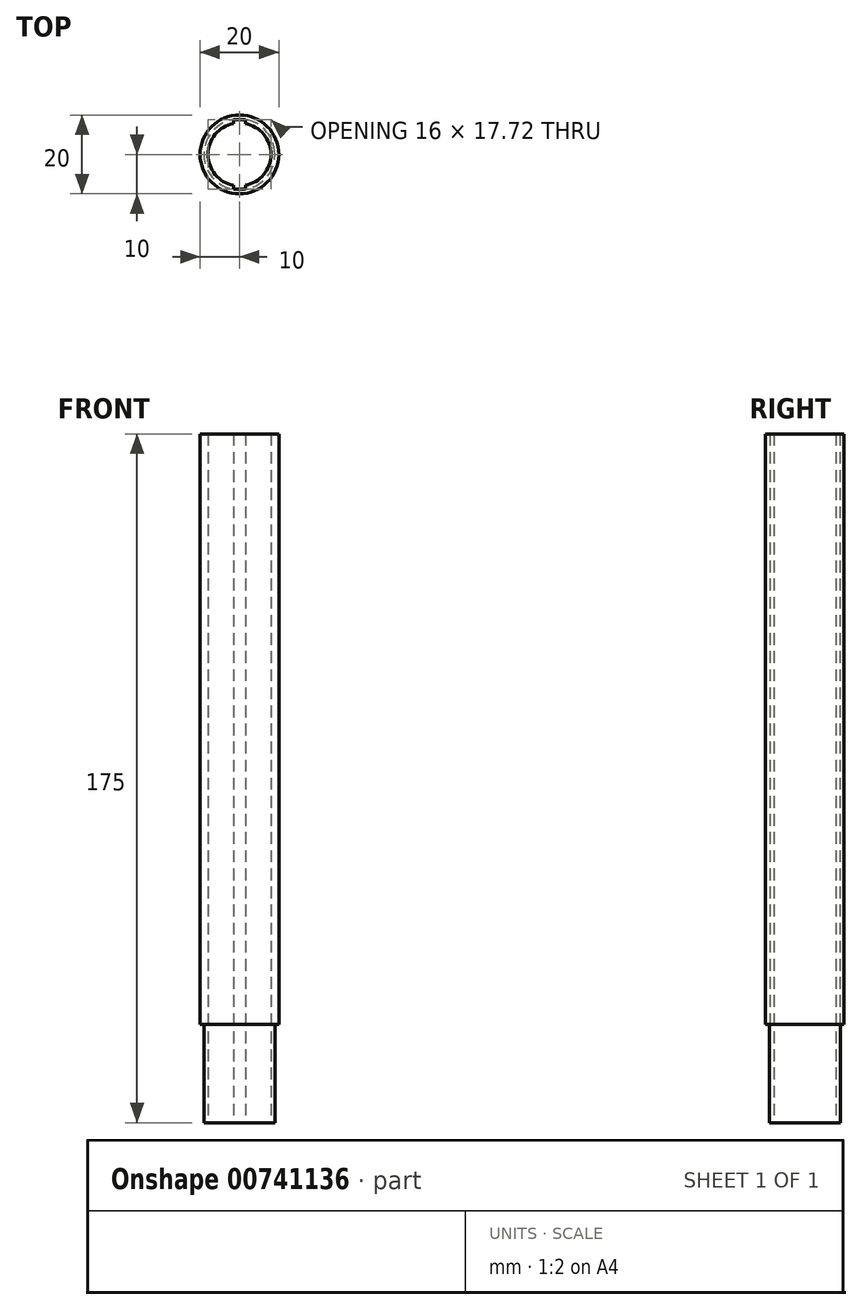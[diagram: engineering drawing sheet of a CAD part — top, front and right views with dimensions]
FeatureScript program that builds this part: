
annotation { "Feature Type Name" : "Feature", "Feature Type Description" : "" }
export const myFeature = defineFeature(function(context is Context, id is Id, definition is map)
    precondition{}
    {
        {
            var Q0;
            Q0=qCreatedBy(makeId("Top.planeOp"),FACE);
            var sketch = newSketch(context, id + "F0", { "sketchPlane" : qUnion([Q0])});
            skCircle(sketch, "E0", {"center": v(0, 0) * mm, "radius": 10 * mm});
            skCircle(sketch, "E1", {"center": v(0, 0) * mm, "radius": 8 * mm});
            skLineSegment(sketch, "E2", {"start": v(-1.5, -7.86) * mm, "end": v(-1.5, -8.86) * mm});
            skLineSegment(sketch, "E3", {"start": v(-1.5, -8.86) * mm, "end": v(1.5, -8.86) * mm});
            skLineSegment(sketch, "E4", {"start": v(1.5, -8.86) * mm, "end": v(1.5, -7.86) * mm});
            skLineSegment(sketch, "E5", {"start": v(-8, 0) * mm, "end": v(8, 0) * mm});
            skLineSegment(sketch, "E6.MirrorCS", {"start": v(1.5, 8.86) * mm, "end": v(1.5, 7.86) * mm});
            skLineSegment(sketch, "E7.MirrorCS", {"start": v(-1.5, 8.86) * mm, "end": v(1.5, 8.86) * mm});
            skLineSegment(sketch, "E8.MirrorCS", {"start": v(-1.5, 7.86) * mm, "end": v(-1.5, 8.86) * mm});
            skCircle(sketch, "E9", {"center": v(0, 0) * mm, "radius": 9 * mm});
            skSolve(sketch);
        }
        {
            var Q0;
            Q0=makeQuery(id+"F0.imprint","IMPRINT",FACE,{"disambiguationData":[TD([[makeQuery(id+"F0.imprint","IMPRINT",EDGE,{"derivedFrom":sQuery(id+"F0.wireOp",EDGE,"E0")}),1.0]])]});
            var Q1;
            {var subQ3=sQuery(id+"F0.wireOp",EDGE,"E2");Q1=makeQuery(id+"F0.imprint","IMPRINT",FACE,{"disambiguationData":[TD([[makeQuery(id+"F0.imprint","IMPRINT",EDGE,{"derivedFrom":subQ3}),-1.0]])]});}
            extrude(context, id + "F1", {"entities" : qUnion([Q0, Q1]), "depth" : 150 * mm, "offsetDistance" : 25 * mm});
        }
        {
            var Q0;
            {var subQ3=sQuery(id+"F0.wireOp",EDGE,"E2");Q0=makeQuery(id+"F0.imprint","IMPRINT",FACE,{"disambiguationData":[TD([[makeQuery(id+"F0.imprint","IMPRINT",EDGE,{"derivedFrom":subQ3}),-1.0]])]});}
            extrude(context, id + "F2", {"entities" : qUnion([Q0]), "operationType" : NewBodyOperationType.ADD, "oppositeDirection" : true, "depth" : 25 * mm, "offsetDistance" : 25 * mm});
        }
    });
